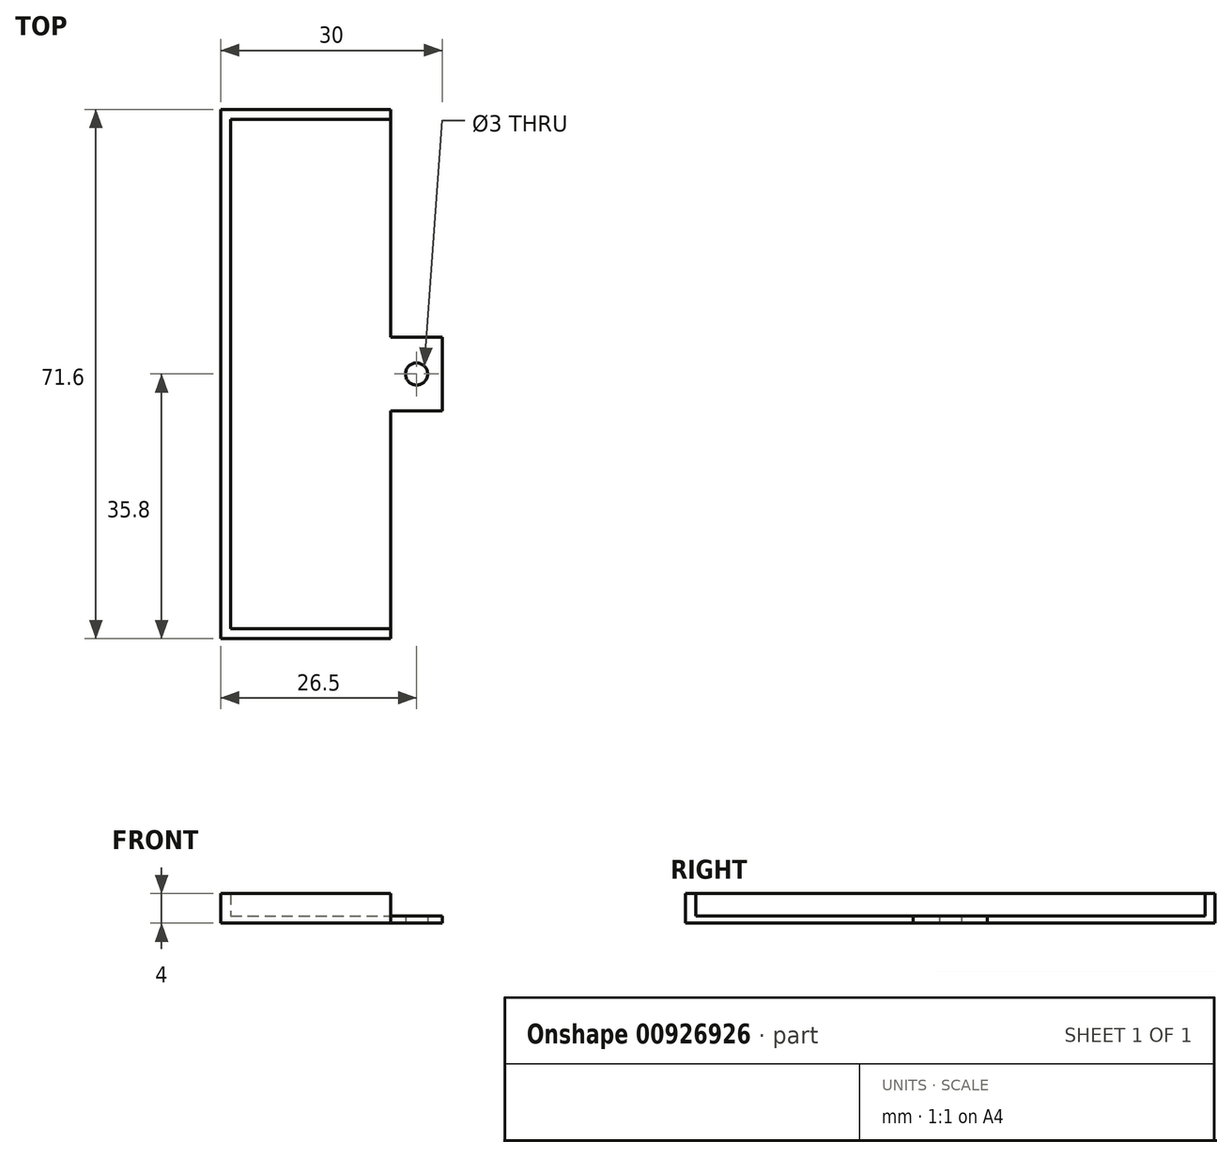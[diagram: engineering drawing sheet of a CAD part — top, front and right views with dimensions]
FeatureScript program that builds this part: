
annotation { "Feature Type Name" : "Feature", "Feature Type Description" : "" }
export const myFeature = defineFeature(function(context is Context, id is Id, definition is map)
    precondition{}
    {
        {
            var Q0;
            Q0=qCreatedBy(makeId("Top.planeOp"),FACE);
            var sketch = newSketch(context, id + "F0", { "sketchPlane" : qUnion([Q0])});
            skLineSegment(sketch, "E0.bottom", {"start": v(-11.5, 35.8) * mm, "end": v(11.5, 35.8) * mm});
            skLineSegment(sketch, "E0.top", {"start": v(-11.5, -35.8) * mm, "end": v(11.5, -35.8) * mm});
            skLineSegment(sketch, "E0.left", {"start": v(-11.5, 35.8) * mm, "end": v(-11.5, -35.8) * mm});
            skPoint(sketch, "E0.middle", {"position": v(0, 0) * mm});
            skLineSegment(sketch, "E1.0", {"start": v(-10.15, 34.45) * mm, "end": v(-10.15, -34.45) * mm});
            skLineSegment(sketch, "E2", {"start": v(-10.15, 34.45) * mm, "end": v(11.5, 34.45) * mm});
            skLineSegment(sketch, "E3", {"start": v(-10.15, -34.45) * mm, "end": v(11.5, -34.45) * mm});
            skLineSegment(sketch, "E4", {"start": v(11.5, 5) * mm, "end": v(18.5, 5) * mm});
            skLineSegment(sketch, "E5", {"start": v(11.5, -5) * mm, "end": v(18.5, -5) * mm});
            skLineSegment(sketch, "E6", {"start": v(18.5, -5) * mm, "end": v(18.5, 5) * mm});
            skLineSegment(sketch, "E7", {"start": v(11.5, 5) * mm, "end": v(11.5, 35.8) * mm});
            skLineSegment(sketch, "E8", {"start": v(11.5, -5) * mm, "end": v(11.5, -35.8) * mm});
            skCircle(sketch, "E9", {"center": v(15, 0) * mm, "radius": 1.5 * mm});
            skPoint(sketch, "E9.centerSnap0", {"position": v(15, -5) * mm});
            skSolve(sketch);
        }
        {
            var Q0;
            {var subQ3=sQuery(id+"F0.wireOp",EDGE,"E0.bottom");Q0=makeQuery(id+"F0.imprint","IMPRINT",FACE,{"disambiguationData":[TD([[makeQuery(id+"F0.imprint","IMPRINT",EDGE,{"derivedFrom":subQ3}),-1.0]])]});}
            extrude(context, id + "F1", {"entities" : qUnion([Q0]), "depth" : 4 * mm, "offsetDistance" : 25 * mm});
        }
        {
            var Q0;
            Q0=makeQuery(id+"F0.imprint","IMPRINT",FACE,{"disambiguationData":[TD([[makeQuery(id+"F0.imprint","IMPRINT",EDGE,{"derivedFrom":sQuery(id+"F0.wireOp",EDGE,"E1.0")}),1.0]])]});
            extrude(context, id + "F2", {"entities" : qUnion([Q0]), "operationType" : NewBodyOperationType.ADD, "depth" : 1 * mm, "offsetDistance" : 25 * mm});
        }
    });
